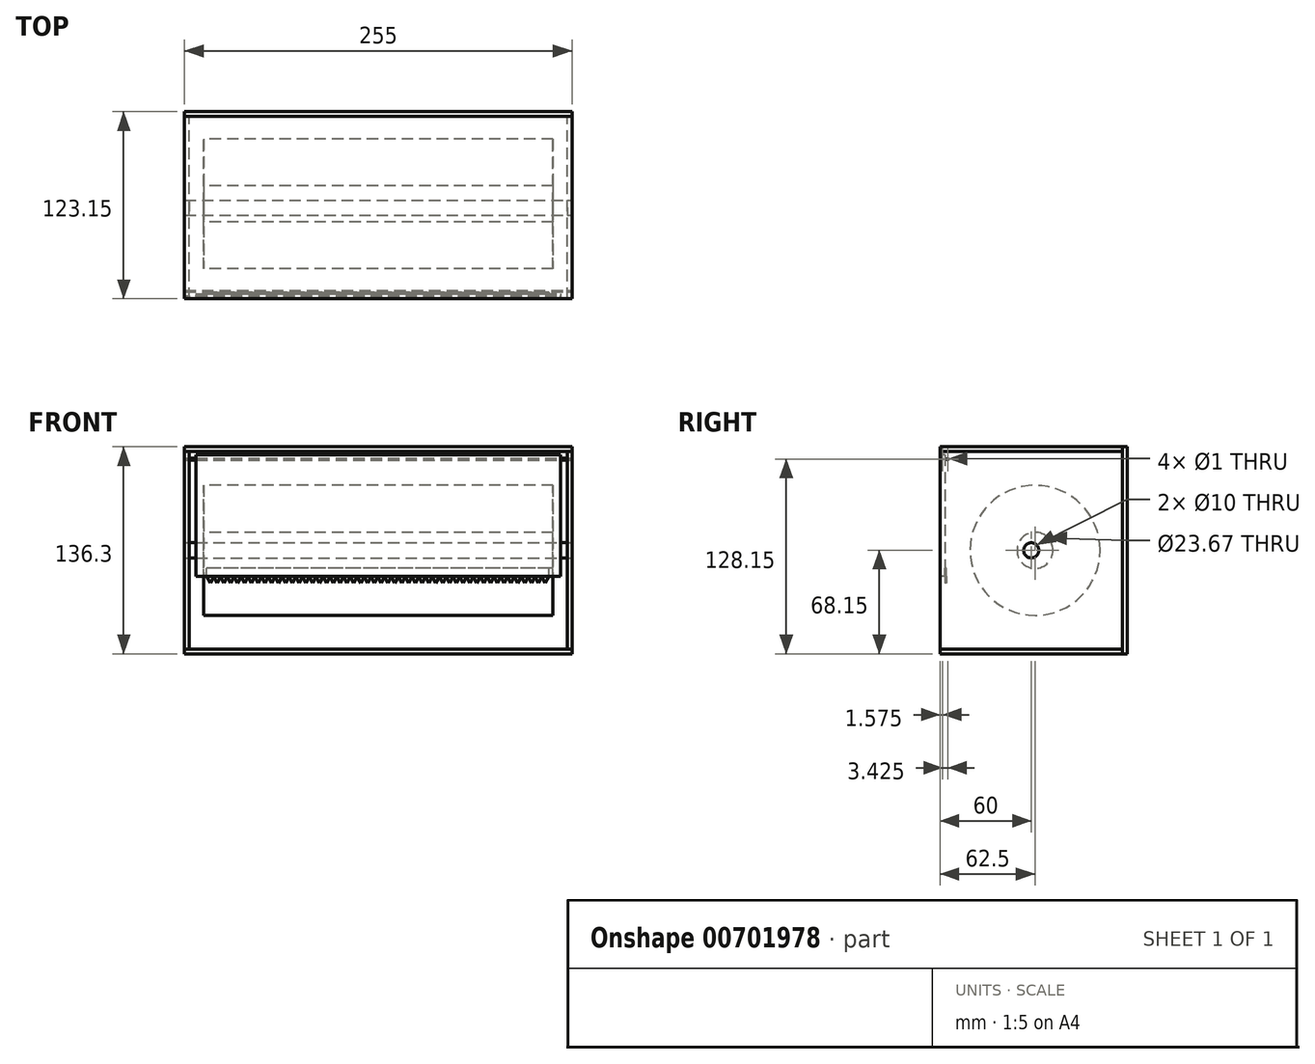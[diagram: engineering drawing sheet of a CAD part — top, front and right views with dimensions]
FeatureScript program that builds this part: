
annotation { "Feature Type Name" : "Feature", "Feature Type Description" : "" }
export const myFeature = defineFeature(function(context is Context, id is Id, definition is map)
    precondition{}
    {
        {
            assignVariable(context, id + "F0", {"name" : "x", "anyValue" : 3.15});
        }
        {
            var Q0;
            Q0=qCreatedBy(makeId("Top.planeOp"),FACE);
            var sketch = newSketch(context, id + "F1", { "sketchPlane" : qUnion([Q0])});
            skLineSegment(sketch, "E0.bottom", {"start": v(0, 0) * mm, "end": v(255, 0) * mm});
            skLineSegment(sketch, "E0.top", {"start": v(0, 120) * mm, "end": v(255, 120) * mm});
            skLineSegment(sketch, "E0.left", {"start": v(0, 0) * mm, "end": v(0, 120) * mm});
            skLineSegment(sketch, "E0.right", {"start": v(255, 0) * mm, "end": v(255, 120) * mm});
            skSolve(sketch);
        }
        {
            var Q0;
            Q0=qSketchRegion(id+"F1",true);
            extrude(context, id + "F2", {"entities" : qUnion([Q0]), "depth" : (getVariable(context, 'x')) * mm, "offsetDistance" : 25 * mm});
        }
        {
            var Q0;
            Q0=makeQuery(id+"F2.opExtrude","SWEPT_FACE",FACE,{"disambiguationData":[OSD([sQuery(id+"F1.wireOp",EDGE,"E0.left")])]});
            var sketch = newSketch(context, id + "F3", { "sketchPlane" : qUnion([Q0])});
            skLineSegment(sketch, "E1.top", {"start": v(0, 133.15) * mm, "end": v(-120, 133.15) * mm});
            skLineSegment(sketch, "E1.left", {"start": v(0, 3.15) * mm, "end": v(0, 133.15) * mm});
            skLineSegment(sketch, "E2", {"start": v(0, 3.15) * mm, "end": v(-120, 3.15) * mm});
            skLineSegment(sketch, "E3", {"start": v(-120, 3.15) * mm, "end": v(-120, 133.15) * mm});
            skSolve(sketch);
        }
        {
            var Q0;
            Q0=qSketchRegion(id+"F3",true);
            extrude(context, id + "F4", {"entities" : qUnion([Q0]), "oppositeDirection" : true, "depth" : (getVariable(context, 'x')) * mm, "offsetDistance" : 25 * mm});
        }
        {
            var Q0;
            Q0=makeQuery(id+"F2.opExtrude","SWEPT_BODY",BODY,{"disambiguationData":[OSD([sQuery(id+"F1.wireOp",EDGE,"E0.bottom"),sQuery(id+"F1.wireOp",EDGE,"E0.top"),sQuery(id+"F1.wireOp",EDGE,"E0.left"),sQuery(id+"F1.wireOp",EDGE,"E0.right")])]});
            transform(context, id + "F5", {"entities" : qUnion([Q0]), "transformType" : TransformType.TRANSLATION_3D, "dx" : 0 * mm, "dy" : 0 * mm, "dz" : 133.15 * mm, "makeCopy" : true});
        }
        {
            var Q0;
            Q0=makeQuery(id+"F4.opExtrude","SWEPT_BODY",BODY,{"disambiguationData":[OSD([sQuery(id+"F3.wireOp",EDGE,"E1.top"),sQuery(id+"F3.wireOp",EDGE,"E1.left"),sQuery(id+"F3.wireOp",EDGE,"E2"),sQuery(id+"F3.wireOp",EDGE,"E3")])]});
            transform(context, id + "F6", {"entities" : qUnion([Q0]), "transformType" : TransformType.TRANSLATION_3D, "dx" : (263.7 + 3.15 - 15) * mm, "dy" : 0 * mm, "dz" : 0 * mm, "makeCopy" : true});
        }
        {
            var Q0;
            Q0=makeQuery(id+"F5.opPattern","COPY",FACE,{"derivedFrom":makeQuery(id+"F2.opExtrude","SWEPT_FACE",FACE,{"disambiguationData":[OSD([sQuery(id+"F1.wireOp",EDGE,"E0.top")])]}),"instanceName":"1"});
            var sketch = newSketch(context, id + "F7", { "sketchPlane" : qUnion([Q0])});
            skLineSegment(sketch, "E4.bottom", {"start": v(-255, 136.3) * mm, "end": v(0, 136.3) * mm});
            skLineSegment(sketch, "E4.top", {"start": v(-255, 0) * mm, "end": v(0, 0) * mm});
            skLineSegment(sketch, "E4.left", {"start": v(-255, 136.3) * mm, "end": v(-255, 0) * mm});
            skLineSegment(sketch, "E4.right", {"start": v(0, 136.3) * mm, "end": v(0, 0) * mm});
            skSolve(sketch);
        }
        {
            var Q0;
            Q0=qSketchRegion(id+"F7",true);
            extrude(context, id + "F8", {"entities" : qUnion([Q0]), "depth" : (getVariable(context, 'x')) * mm, "offsetDistance" : 25 * mm});
        }
        {
            var Q0;
            Q0=makeQuery(id+"F2.opExtrude","CAP_EDGE",EDGE,{"disambiguationData":[OSD([sQuery(id+"F1.wireOp",EDGE,"E0.bottom")])],"isStart":false});
            cPoint(context, id + "F9", {"entities" : qUnion([Q0]), "parameter" : 0.5});
        }
        {
            var Q0;
            Q0=makeQuery(id+"F4.opExtrude","CAP_FACE",FACE,{"disambiguationData":[OSD([sQuery(id+"F3.wireOp",EDGE,"E1.top"),sQuery(id+"F3.wireOp",EDGE,"E1.left"),sQuery(id+"F3.wireOp",EDGE,"E2"),sQuery(id+"F3.wireOp",EDGE,"E3")])],"isStart":false});
            var Q1;
            Q1 = qCreatedBy(id + "F9" ,VERTEX);
            cPlane(context, id + "F10", {"entities" : qUnion([Q0, Q1]), "cplaneType" : CPlaneType.PLANE_POINT, "offset" : 25 * mm, "width" : 150 * mm, "height" : 150 * mm});
        }
        {
            var Q0;
            Q0=qCreatedBy(id+"F10.planeOp",FACE);
            var sketch = newSketch(context, id + "F11", { "sketchPlane" : qUnion([Q0])});
            skCircle(sketch, "E5", {"center": v(62.5, 68.15) * mm, "radius": 11.84 * mm});
            skCircle(sketch, "E6", {"center": v(62.5, 68.15) * mm, "radius": 42.82 * mm});
            skLineSegment(sketch, "E7", {"start": v(5, 133.15) * mm, "end": v(5, 3.15) * mm, "construction": true});
            skLineSegment(sketch, "E8", {"start": v(5, 68.15) * mm, "end": v(62.5, 68.15) * mm, "construction": true});
            skLineSegment(sketch, "E9", {"start": v(62.5, 68.15) * mm, "end": v(120, 68.15) * mm, "construction": true});
            skSolve(sketch);
        }
        {
            var Q0;
            Q0 = qSketchRegion(id + "F11", true);
            extrude(context, id + "F12", {"entities" : qUnion([Q0]), "depth" : (230 / 2) * mm, "offsetDistance" : 25 * mm, "hasSecondDirection" : true, "secondDirectionOppositeDirection" : true, "secondDirectionDepth" : 115 * mm});
        }
        {
            var Q0;
            Q0=makeQuery(id+"F5.opPattern","COPY",FACE,{"derivedFrom":makeQuery(id+"F2.opExtrude","SWEPT_FACE",FACE,{"disambiguationData":[OSD([sQuery(id+"F1.wireOp",EDGE,"E0.bottom")])]}),"instanceName":"1"});
            var sketch = newSketch(context, id + "F13", { "sketchPlane" : qUnion([Q0])});
            skLineSegment(sketch, "E10.bottom", {"start": v(7.5, 131.15) * mm, "end": v(247.5, 131.15) * mm});
            skLineSegment(sketch, "E10.top", {"start": v(7.5, 51.15) * mm, "end": v(247.5, 51.15) * mm});
            skLineSegment(sketch, "E10.left", {"start": v(7.5, 131.15) * mm, "end": v(7.5, 51.15) * mm});
            skLineSegment(sketch, "E10.right", {"start": v(247.5, 131.15) * mm, "end": v(247.5, 51.15) * mm});
            skLineSegment(sketch, "E11", {"start": v(127.5, 131.15) * mm, "end": v(127.5, 133.15) * mm, "construction": true});
            skSolve(sketch);
        }
        {
            var Q0;
            Q0 = qSketchRegion(id + "F13", true);
            extrude(context, id + "F14", {"entities" : qUnion([Q0]), "oppositeDirection" : true, "depth" : (getVariable(context, 'x')) * mm, "offsetDistance" : 25 * mm});
        }
        {
            var Q0;
            Q0=makeQuery(id+"F14.opExtrude","CAP_FACE",FACE,{"disambiguationData":[OSD([sQuery(id+"F13.wireOp",EDGE,"E10.bottom"),sQuery(id+"F13.wireOp",EDGE,"E10.top"),sQuery(id+"F13.wireOp",EDGE,"E10.left"),sQuery(id+"F13.wireOp",EDGE,"E10.right")])],"isStart":false});
            var sketch = newSketch(context, id + "F15", { "sketchPlane" : qUnion([Q0])});
            skCircle(sketch, "E12.cCircle", {"center": v(-237.44, 49.65) * mm, "radius": 1.5 * mm, "construction": true});
            skLineSegment(sketch, "E12.0", {"start": v(-234.85, 51.15) * mm, "end": v(-237.44, 46.65) * mm});
            skLineSegment(sketch, "E12.1", {"start": v(-237.44, 46.65) * mm, "end": v(-240.04, 51.15) * mm});
            skLineSegment(sketch, "E12.2", {"start": v(-240.04, 51.15) * mm, "end": v(-234.85, 51.15) * mm});
            skLineSegment(sketch, "E13.1.0.0", {"start": v(-230.35, 51.15) * mm, "end": v(-232.94, 46.65) * mm});
            skLineSegment(sketch, "E13.1.0.1", {"start": v(-232.94, 46.65) * mm, "end": v(-235.54, 51.15) * mm});
            skLineSegment(sketch, "E13.1.0.2", {"start": v(-235.54, 51.15) * mm, "end": v(-230.35, 51.15) * mm});
            skLineSegment(sketch, "E13.2.0.0", {"start": v(-225.85, 51.15) * mm, "end": v(-228.44, 46.65) * mm});
            skLineSegment(sketch, "E13.2.0.1", {"start": v(-228.44, 46.65) * mm, "end": v(-231.04, 51.15) * mm});
            skLineSegment(sketch, "E13.2.0.2", {"start": v(-231.04, 51.15) * mm, "end": v(-225.85, 51.15) * mm});
            skLineSegment(sketch, "E13.3.0.0", {"start": v(-221.35, 51.15) * mm, "end": v(-223.94, 46.65) * mm});
            skLineSegment(sketch, "E13.3.0.1", {"start": v(-223.94, 46.65) * mm, "end": v(-226.54, 51.15) * mm});
            skLineSegment(sketch, "E13.3.0.2", {"start": v(-226.54, 51.15) * mm, "end": v(-221.35, 51.15) * mm});
            skLineSegment(sketch, "E13.4.0.0", {"start": v(-216.85, 51.15) * mm, "end": v(-219.44, 46.65) * mm});
            skLineSegment(sketch, "E13.4.0.1", {"start": v(-219.44, 46.65) * mm, "end": v(-222.04, 51.15) * mm});
            skLineSegment(sketch, "E13.4.0.2", {"start": v(-222.04, 51.15) * mm, "end": v(-216.85, 51.15) * mm});
            skLineSegment(sketch, "E13.5.0.0", {"start": v(-212.35, 51.15) * mm, "end": v(-214.94, 46.65) * mm});
            skLineSegment(sketch, "E13.5.0.1", {"start": v(-214.94, 46.65) * mm, "end": v(-217.54, 51.15) * mm});
            skLineSegment(sketch, "E13.5.0.2", {"start": v(-217.54, 51.15) * mm, "end": v(-212.35, 51.15) * mm});
            skLineSegment(sketch, "E13.6.0.0", {"start": v(-207.85, 51.15) * mm, "end": v(-210.44, 46.65) * mm});
            skLineSegment(sketch, "E13.6.0.1", {"start": v(-210.44, 46.65) * mm, "end": v(-213.04, 51.15) * mm});
            skLineSegment(sketch, "E13.6.0.2", {"start": v(-213.04, 51.15) * mm, "end": v(-207.85, 51.15) * mm});
            skLineSegment(sketch, "E13.7.0.0", {"start": v(-203.35, 51.15) * mm, "end": v(-205.94, 46.65) * mm});
            skLineSegment(sketch, "E13.7.0.1", {"start": v(-205.94, 46.65) * mm, "end": v(-208.54, 51.15) * mm});
            skLineSegment(sketch, "E13.7.0.2", {"start": v(-208.54, 51.15) * mm, "end": v(-203.35, 51.15) * mm});
            skLineSegment(sketch, "E13.8.0.0", {"start": v(-198.85, 51.15) * mm, "end": v(-201.44, 46.65) * mm});
            skLineSegment(sketch, "E13.8.0.1", {"start": v(-201.44, 46.65) * mm, "end": v(-204.04, 51.15) * mm});
            skLineSegment(sketch, "E13.8.0.2", {"start": v(-204.04, 51.15) * mm, "end": v(-198.85, 51.15) * mm});
            skLineSegment(sketch, "E13.9.0.0", {"start": v(-194.35, 51.15) * mm, "end": v(-196.94, 46.65) * mm});
            skLineSegment(sketch, "E13.9.0.1", {"start": v(-196.94, 46.65) * mm, "end": v(-199.54, 51.15) * mm});
            skLineSegment(sketch, "E13.9.0.2", {"start": v(-199.54, 51.15) * mm, "end": v(-194.35, 51.15) * mm});
            skLineSegment(sketch, "E13.10.0.0", {"start": v(-189.85, 51.15) * mm, "end": v(-192.44, 46.65) * mm});
            skLineSegment(sketch, "E13.10.0.1", {"start": v(-192.44, 46.65) * mm, "end": v(-195.04, 51.15) * mm});
            skLineSegment(sketch, "E13.10.0.2", {"start": v(-195.04, 51.15) * mm, "end": v(-189.85, 51.15) * mm});
            skLineSegment(sketch, "E13.11.0.0", {"start": v(-185.35, 51.15) * mm, "end": v(-187.94, 46.65) * mm});
            skLineSegment(sketch, "E13.11.0.1", {"start": v(-187.94, 46.65) * mm, "end": v(-190.54, 51.15) * mm});
            skLineSegment(sketch, "E13.11.0.2", {"start": v(-190.54, 51.15) * mm, "end": v(-185.35, 51.15) * mm});
            skLineSegment(sketch, "E13.12.0.0", {"start": v(-180.85, 51.15) * mm, "end": v(-183.44, 46.65) * mm});
            skLineSegment(sketch, "E13.12.0.1", {"start": v(-183.44, 46.65) * mm, "end": v(-186.04, 51.15) * mm});
            skLineSegment(sketch, "E13.12.0.2", {"start": v(-186.04, 51.15) * mm, "end": v(-180.85, 51.15) * mm});
            skLineSegment(sketch, "E13.13.0.0", {"start": v(-176.35, 51.15) * mm, "end": v(-178.94, 46.65) * mm});
            skLineSegment(sketch, "E13.13.0.1", {"start": v(-178.94, 46.65) * mm, "end": v(-181.54, 51.15) * mm});
            skLineSegment(sketch, "E13.13.0.2", {"start": v(-181.54, 51.15) * mm, "end": v(-176.35, 51.15) * mm});
            skLineSegment(sketch, "E13.14.0.0", {"start": v(-171.85, 51.15) * mm, "end": v(-174.44, 46.65) * mm});
            skLineSegment(sketch, "E13.14.0.1", {"start": v(-174.44, 46.65) * mm, "end": v(-177.04, 51.15) * mm});
            skLineSegment(sketch, "E13.14.0.2", {"start": v(-177.04, 51.15) * mm, "end": v(-171.85, 51.15) * mm});
            skLineSegment(sketch, "E13.15.0.0", {"start": v(-167.35, 51.15) * mm, "end": v(-169.94, 46.65) * mm});
            skLineSegment(sketch, "E13.15.0.1", {"start": v(-169.94, 46.65) * mm, "end": v(-172.54, 51.15) * mm});
            skLineSegment(sketch, "E13.15.0.2", {"start": v(-172.54, 51.15) * mm, "end": v(-167.35, 51.15) * mm});
            skLineSegment(sketch, "E13.16.0.0", {"start": v(-162.85, 51.15) * mm, "end": v(-165.44, 46.65) * mm});
            skLineSegment(sketch, "E13.16.0.1", {"start": v(-165.44, 46.65) * mm, "end": v(-168.04, 51.15) * mm});
            skLineSegment(sketch, "E13.16.0.2", {"start": v(-168.04, 51.15) * mm, "end": v(-162.85, 51.15) * mm});
            skLineSegment(sketch, "E13.17.0.0", {"start": v(-158.35, 51.15) * mm, "end": v(-160.94, 46.65) * mm});
            skLineSegment(sketch, "E13.17.0.1", {"start": v(-160.94, 46.65) * mm, "end": v(-163.54, 51.15) * mm});
            skLineSegment(sketch, "E13.17.0.2", {"start": v(-163.54, 51.15) * mm, "end": v(-158.35, 51.15) * mm});
            skLineSegment(sketch, "E13.18.0.0", {"start": v(-153.85, 51.15) * mm, "end": v(-156.44, 46.65) * mm});
            skLineSegment(sketch, "E13.18.0.1", {"start": v(-156.44, 46.65) * mm, "end": v(-159.04, 51.15) * mm});
            skLineSegment(sketch, "E13.18.0.2", {"start": v(-159.04, 51.15) * mm, "end": v(-153.85, 51.15) * mm});
            skLineSegment(sketch, "E13.19.0.0", {"start": v(-149.35, 51.15) * mm, "end": v(-151.94, 46.65) * mm});
            skLineSegment(sketch, "E13.19.0.1", {"start": v(-151.94, 46.65) * mm, "end": v(-154.54, 51.15) * mm});
            skLineSegment(sketch, "E13.19.0.2", {"start": v(-154.54, 51.15) * mm, "end": v(-149.35, 51.15) * mm});
            skLineSegment(sketch, "E13.20.0.0", {"start": v(-144.85, 51.15) * mm, "end": v(-147.44, 46.65) * mm});
            skLineSegment(sketch, "E13.20.0.1", {"start": v(-147.44, 46.65) * mm, "end": v(-150.04, 51.15) * mm});
            skLineSegment(sketch, "E13.20.0.2", {"start": v(-150.04, 51.15) * mm, "end": v(-144.85, 51.15) * mm});
            skLineSegment(sketch, "E13.21.0.0", {"start": v(-140.35, 51.15) * mm, "end": v(-142.94, 46.65) * mm});
            skLineSegment(sketch, "E13.21.0.1", {"start": v(-142.94, 46.65) * mm, "end": v(-145.54, 51.15) * mm});
            skLineSegment(sketch, "E13.21.0.2", {"start": v(-145.54, 51.15) * mm, "end": v(-140.35, 51.15) * mm});
            skLineSegment(sketch, "E13.22.0.0", {"start": v(-135.85, 51.15) * mm, "end": v(-138.44, 46.65) * mm});
            skLineSegment(sketch, "E13.22.0.1", {"start": v(-138.44, 46.65) * mm, "end": v(-141.04, 51.15) * mm});
            skLineSegment(sketch, "E13.22.0.2", {"start": v(-141.04, 51.15) * mm, "end": v(-135.85, 51.15) * mm});
            skLineSegment(sketch, "E13.23.0.0", {"start": v(-131.35, 51.15) * mm, "end": v(-133.94, 46.65) * mm});
            skLineSegment(sketch, "E13.23.0.1", {"start": v(-133.94, 46.65) * mm, "end": v(-136.54, 51.15) * mm});
            skLineSegment(sketch, "E13.23.0.2", {"start": v(-136.54, 51.15) * mm, "end": v(-131.35, 51.15) * mm});
            skLineSegment(sketch, "E13.24.0.0", {"start": v(-126.85, 51.15) * mm, "end": v(-129.44, 46.65) * mm});
            skLineSegment(sketch, "E13.24.0.1", {"start": v(-129.44, 46.65) * mm, "end": v(-132.04, 51.15) * mm});
            skLineSegment(sketch, "E13.24.0.2", {"start": v(-132.04, 51.15) * mm, "end": v(-126.85, 51.15) * mm});
            skLineSegment(sketch, "E13.25.0.0", {"start": v(-122.35, 51.15) * mm, "end": v(-124.94, 46.65) * mm});
            skLineSegment(sketch, "E13.25.0.1", {"start": v(-124.94, 46.65) * mm, "end": v(-127.54, 51.15) * mm});
            skLineSegment(sketch, "E13.25.0.2", {"start": v(-127.54, 51.15) * mm, "end": v(-122.35, 51.15) * mm});
            skLineSegment(sketch, "E13.26.0.0", {"start": v(-117.85, 51.15) * mm, "end": v(-120.44, 46.65) * mm});
            skLineSegment(sketch, "E13.26.0.1", {"start": v(-120.44, 46.65) * mm, "end": v(-123.04, 51.15) * mm});
            skLineSegment(sketch, "E13.26.0.2", {"start": v(-123.04, 51.15) * mm, "end": v(-117.85, 51.15) * mm});
            skLineSegment(sketch, "E13.27.0.0", {"start": v(-113.35, 51.15) * mm, "end": v(-115.94, 46.65) * mm});
            skLineSegment(sketch, "E13.27.0.1", {"start": v(-115.94, 46.65) * mm, "end": v(-118.54, 51.15) * mm});
            skLineSegment(sketch, "E13.27.0.2", {"start": v(-118.54, 51.15) * mm, "end": v(-113.35, 51.15) * mm});
            skLineSegment(sketch, "E13.28.0.0", {"start": v(-108.85, 51.15) * mm, "end": v(-111.44, 46.65) * mm});
            skLineSegment(sketch, "E13.28.0.1", {"start": v(-111.44, 46.65) * mm, "end": v(-114.04, 51.15) * mm});
            skLineSegment(sketch, "E13.28.0.2", {"start": v(-114.04, 51.15) * mm, "end": v(-108.85, 51.15) * mm});
            skLineSegment(sketch, "E13.29.0.0", {"start": v(-104.35, 51.15) * mm, "end": v(-106.94, 46.65) * mm});
            skLineSegment(sketch, "E13.29.0.1", {"start": v(-106.94, 46.65) * mm, "end": v(-109.54, 51.15) * mm});
            skLineSegment(sketch, "E13.29.0.2", {"start": v(-109.54, 51.15) * mm, "end": v(-104.35, 51.15) * mm});
            skLineSegment(sketch, "E13.30.0.0", {"start": v(-99.85, 51.15) * mm, "end": v(-102.44, 46.65) * mm});
            skLineSegment(sketch, "E13.30.0.1", {"start": v(-102.44, 46.65) * mm, "end": v(-105.04, 51.15) * mm});
            skLineSegment(sketch, "E13.30.0.2", {"start": v(-105.04, 51.15) * mm, "end": v(-99.85, 51.15) * mm});
            skLineSegment(sketch, "E13.31.0.0", {"start": v(-95.35, 51.15) * mm, "end": v(-97.94, 46.65) * mm});
            skLineSegment(sketch, "E13.31.0.1", {"start": v(-97.94, 46.65) * mm, "end": v(-100.54, 51.15) * mm});
            skLineSegment(sketch, "E13.31.0.2", {"start": v(-100.54, 51.15) * mm, "end": v(-95.35, 51.15) * mm});
            skLineSegment(sketch, "E13.32.0.0", {"start": v(-90.85, 51.15) * mm, "end": v(-93.44, 46.65) * mm});
            skLineSegment(sketch, "E13.32.0.1", {"start": v(-93.44, 46.65) * mm, "end": v(-96.04, 51.15) * mm});
            skLineSegment(sketch, "E13.32.0.2", {"start": v(-96.04, 51.15) * mm, "end": v(-90.85, 51.15) * mm});
            skLineSegment(sketch, "E13.33.0.0", {"start": v(-86.35, 51.15) * mm, "end": v(-88.94, 46.65) * mm});
            skLineSegment(sketch, "E13.33.0.1", {"start": v(-88.94, 46.65) * mm, "end": v(-91.54, 51.15) * mm});
            skLineSegment(sketch, "E13.33.0.2", {"start": v(-91.54, 51.15) * mm, "end": v(-86.35, 51.15) * mm});
            skLineSegment(sketch, "E13.34.0.0", {"start": v(-81.85, 51.15) * mm, "end": v(-84.44, 46.65) * mm});
            skLineSegment(sketch, "E13.34.0.1", {"start": v(-84.44, 46.65) * mm, "end": v(-87.04, 51.15) * mm});
            skLineSegment(sketch, "E13.34.0.2", {"start": v(-87.04, 51.15) * mm, "end": v(-81.85, 51.15) * mm});
            skLineSegment(sketch, "E13.35.0.0", {"start": v(-77.35, 51.15) * mm, "end": v(-79.94, 46.65) * mm});
            skLineSegment(sketch, "E13.35.0.1", {"start": v(-79.94, 46.65) * mm, "end": v(-82.54, 51.15) * mm});
            skLineSegment(sketch, "E13.35.0.2", {"start": v(-82.54, 51.15) * mm, "end": v(-77.35, 51.15) * mm});
            skLineSegment(sketch, "E13.36.0.0", {"start": v(-72.85, 51.15) * mm, "end": v(-75.44, 46.65) * mm});
            skLineSegment(sketch, "E13.36.0.1", {"start": v(-75.44, 46.65) * mm, "end": v(-78.04, 51.15) * mm});
            skLineSegment(sketch, "E13.36.0.2", {"start": v(-78.04, 51.15) * mm, "end": v(-72.85, 51.15) * mm});
            skLineSegment(sketch, "E13.37.0.0", {"start": v(-68.35, 51.15) * mm, "end": v(-70.94, 46.65) * mm});
            skLineSegment(sketch, "E13.37.0.1", {"start": v(-70.94, 46.65) * mm, "end": v(-73.54, 51.15) * mm});
            skLineSegment(sketch, "E13.37.0.2", {"start": v(-73.54, 51.15) * mm, "end": v(-68.35, 51.15) * mm});
            skLineSegment(sketch, "E13.38.0.0", {"start": v(-63.85, 51.15) * mm, "end": v(-66.44, 46.65) * mm});
            skLineSegment(sketch, "E13.38.0.1", {"start": v(-66.44, 46.65) * mm, "end": v(-69.04, 51.15) * mm});
            skLineSegment(sketch, "E13.38.0.2", {"start": v(-69.04, 51.15) * mm, "end": v(-63.85, 51.15) * mm});
            skLineSegment(sketch, "E13.39.0.0", {"start": v(-59.35, 51.15) * mm, "end": v(-61.94, 46.65) * mm});
            skLineSegment(sketch, "E13.39.0.1", {"start": v(-61.94, 46.65) * mm, "end": v(-64.54, 51.15) * mm});
            skLineSegment(sketch, "E13.39.0.2", {"start": v(-64.54, 51.15) * mm, "end": v(-59.35, 51.15) * mm});
            skLineSegment(sketch, "E13.40.0.0", {"start": v(-54.85, 51.15) * mm, "end": v(-57.44, 46.65) * mm});
            skLineSegment(sketch, "E13.40.0.1", {"start": v(-57.44, 46.65) * mm, "end": v(-60.04, 51.15) * mm});
            skLineSegment(sketch, "E13.40.0.2", {"start": v(-60.04, 51.15) * mm, "end": v(-54.85, 51.15) * mm});
            skLineSegment(sketch, "E13.41.0.0", {"start": v(-50.35, 51.15) * mm, "end": v(-52.94, 46.65) * mm});
            skLineSegment(sketch, "E13.41.0.1", {"start": v(-52.94, 46.65) * mm, "end": v(-55.54, 51.15) * mm});
            skLineSegment(sketch, "E13.41.0.2", {"start": v(-55.54, 51.15) * mm, "end": v(-50.35, 51.15) * mm});
            skLineSegment(sketch, "E13.42.0.0", {"start": v(-45.85, 51.15) * mm, "end": v(-48.44, 46.65) * mm});
            skLineSegment(sketch, "E13.42.0.1", {"start": v(-48.44, 46.65) * mm, "end": v(-51.04, 51.15) * mm});
            skLineSegment(sketch, "E13.42.0.2", {"start": v(-51.04, 51.15) * mm, "end": v(-45.85, 51.15) * mm});
            skLineSegment(sketch, "E13.43.0.0", {"start": v(-41.35, 51.15) * mm, "end": v(-43.94, 46.65) * mm});
            skLineSegment(sketch, "E13.43.0.1", {"start": v(-43.94, 46.65) * mm, "end": v(-46.54, 51.15) * mm});
            skLineSegment(sketch, "E13.43.0.2", {"start": v(-46.54, 51.15) * mm, "end": v(-41.35, 51.15) * mm});
            skLineSegment(sketch, "E13.44.0.0", {"start": v(-36.85, 51.15) * mm, "end": v(-39.44, 46.65) * mm});
            skLineSegment(sketch, "E13.44.0.1", {"start": v(-39.44, 46.65) * mm, "end": v(-42.04, 51.15) * mm});
            skLineSegment(sketch, "E13.44.0.2", {"start": v(-42.04, 51.15) * mm, "end": v(-36.85, 51.15) * mm});
            skLineSegment(sketch, "E13.45.0.0", {"start": v(-32.35, 51.15) * mm, "end": v(-34.94, 46.65) * mm});
            skLineSegment(sketch, "E13.45.0.1", {"start": v(-34.94, 46.65) * mm, "end": v(-37.54, 51.15) * mm});
            skLineSegment(sketch, "E13.45.0.2", {"start": v(-37.54, 51.15) * mm, "end": v(-32.35, 51.15) * mm});
            skLineSegment(sketch, "E13.46.0.0", {"start": v(-27.85, 51.15) * mm, "end": v(-30.44, 46.65) * mm});
            skLineSegment(sketch, "E13.46.0.1", {"start": v(-30.44, 46.65) * mm, "end": v(-33.04, 51.15) * mm});
            skLineSegment(sketch, "E13.46.0.2", {"start": v(-33.04, 51.15) * mm, "end": v(-27.85, 51.15) * mm});
            skLineSegment(sketch, "E13.47.0.0", {"start": v(-23.35, 51.15) * mm, "end": v(-25.94, 46.65) * mm});
            skLineSegment(sketch, "E13.47.0.1", {"start": v(-25.94, 46.65) * mm, "end": v(-28.54, 51.15) * mm});
            skLineSegment(sketch, "E13.47.0.2", {"start": v(-28.54, 51.15) * mm, "end": v(-23.35, 51.15) * mm});
            skLineSegment(sketch, "E13.48.0.0", {"start": v(-18.85, 51.15) * mm, "end": v(-21.44, 46.65) * mm});
            skLineSegment(sketch, "E13.48.0.1", {"start": v(-21.44, 46.65) * mm, "end": v(-24.04, 51.15) * mm});
            skLineSegment(sketch, "E13.48.0.2", {"start": v(-24.04, 51.15) * mm, "end": v(-18.85, 51.15) * mm});
            skLineSegment(sketch, "E13.49.0.0", {"start": v(-14.35, 51.15) * mm, "end": v(-16.94, 46.65) * mm});
            skLineSegment(sketch, "E13.49.0.1", {"start": v(-16.94, 46.65) * mm, "end": v(-19.54, 51.15) * mm});
            skLineSegment(sketch, "E13.49.0.2", {"start": v(-19.54, 51.15) * mm, "end": v(-14.35, 51.15) * mm});
            skLineSegment(sketch, "E13.direction1", {"start": v(-237.44, 46.65) * mm, "end": v(-232.94, 46.65) * mm, "construction": true});
            skLineSegment(sketch, "E14.bottom", {"start": v(-240.04, 51.15) * mm, "end": v(-14.35, 51.15) * mm});
            skLineSegment(sketch, "E14.top", {"start": v(-240.04, 56.28) * mm, "end": v(-14.35, 56.28) * mm});
            skLineSegment(sketch, "E14.left", {"start": v(-240.04, 51.15) * mm, "end": v(-240.04, 56.28) * mm});
            skLineSegment(sketch, "E14.right", {"start": v(-14.35, 51.15) * mm, "end": v(-14.35, 56.28) * mm});
            skSolve(sketch);
        }
        {
            var Q0;
            Q0 = qSketchRegion(id + "F15", true);
            extrude(context, id + "F16", {"entities" : qUnion([Q0]), "depth" : 1 * mm, "offsetDistance" : 25 * mm});
        }
        {
            var Q0;
            Q0=makeQuery(id+"F6.opPattern","COPY",FACE,{"derivedFrom":makeQuery(id+"F4.opExtrude","CAP_FACE",FACE,{"disambiguationData":[OSD([sQuery(id+"F3.wireOp",EDGE,"E1.top"),sQuery(id+"F3.wireOp",EDGE,"E1.left"),sQuery(id+"F3.wireOp",EDGE,"E2"),sQuery(id+"F3.wireOp",EDGE,"E3")])],"isStart":false}),"instanceName":"1"});
            var sketch = newSketch(context, id + "F17", { "sketchPlane" : qUnion([Q0])});
            skCircle(sketch, "E15", {"center": v(60, 68.15) * mm, "radius": 5 * mm});
            skPoint(sketch, "E15.centerSnap0", {"position": v(60, 133.15) * mm});
            skPoint(sketch, "E15.centerSnap1", {"position": v(0, 68.15) * mm});
            skCircle(sketch, "E16", {"center": v(5, 128.15) * mm, "radius": 0.5 * mm});
            skSolve(sketch);
        }
        {
            var Q0;
            Q0 = qSketchRegion(id + "F17", true);
            extrude(context, id + "F18", {"entities" : qUnion([Q0]), "operationType" : NewBodyOperationType.REMOVE, "endBound" : BoundingType.THROUGH_ALL, "oppositeDirection" : true, "depth" : 25 * mm, "offsetDistance" : 25 * mm});
        }
        {
            var Q0;
            Q0=makeQuery(id+"F6.opPattern","COPY",FACE,{"derivedFrom":makeQuery(id+"F4.opExtrude","CAP_FACE",FACE,{"disambiguationData":[OSD([sQuery(id+"F3.wireOp",EDGE,"E1.top"),sQuery(id+"F3.wireOp",EDGE,"E1.left"),sQuery(id+"F3.wireOp",EDGE,"E2"),sQuery(id+"F3.wireOp",EDGE,"E3")])],"isStart":false}),"instanceName":"1"});
            var sketch = newSketch(context, id + "F19", { "sketchPlane" : qUnion([Q0])});
            skCircle(sketch, "E17", {"center": v(60, 68.15) * mm, "radius": 5 * mm});
            skCircle(sketch, "E18", {"center": v(5, 128.15) * mm, "radius": 0.5 * mm});
            skSolve(sketch);
        }
        {
            var Q0;
            Q0 = qSketchRegion(id + "F19", true);
            var Q1;
            Q1=makeQuery(id+"F4.opExtrude","CAP_FACE",FACE,{"disambiguationData":[OSD([sQuery(id+"F3.wireOp",EDGE,"E1.top"),sQuery(id+"F3.wireOp",EDGE,"E1.left"),sQuery(id+"F3.wireOp",EDGE,"E2"),sQuery(id+"F3.wireOp",EDGE,"E3")])],"isStart":true});
            extrude(context, id + "F20", {"entities" : qUnion([Q0]), "endBound" : BoundingType.UP_TO_SURFACE, "oppositeDirection" : true, "depth" : 25 * mm, "endBoundEntityFace" : qUnion([Q1]), "offsetDistance" : 25 * mm});
        }
        {
            var Q0;
            Q0=makeQuery(id+"F14.opExtrude","SWEPT_FACE",FACE,{"disambiguationData":[OSD([sQuery(id+"F13.wireOp",EDGE,"E10.right")])]});
            var sketch = newSketch(context, id + "F21", { "sketchPlane" : qUnion([Q0])});
            skCircle(sketch, "E19", {"center": v(1.57, 128.15) * mm, "radius": 0.5 * mm});
            skSolve(sketch);
        }
        {
            var Q0;
            Q0 = qSketchRegion(id + "F21", true);
            extrude(context, id + "F22", {"entities" : qUnion([Q0]), "operationType" : NewBodyOperationType.REMOVE, "endBound" : BoundingType.THROUGH_ALL, "oppositeDirection" : true, "depth" : 25 * mm, "offsetDistance" : 25 * mm});
        }
    });
